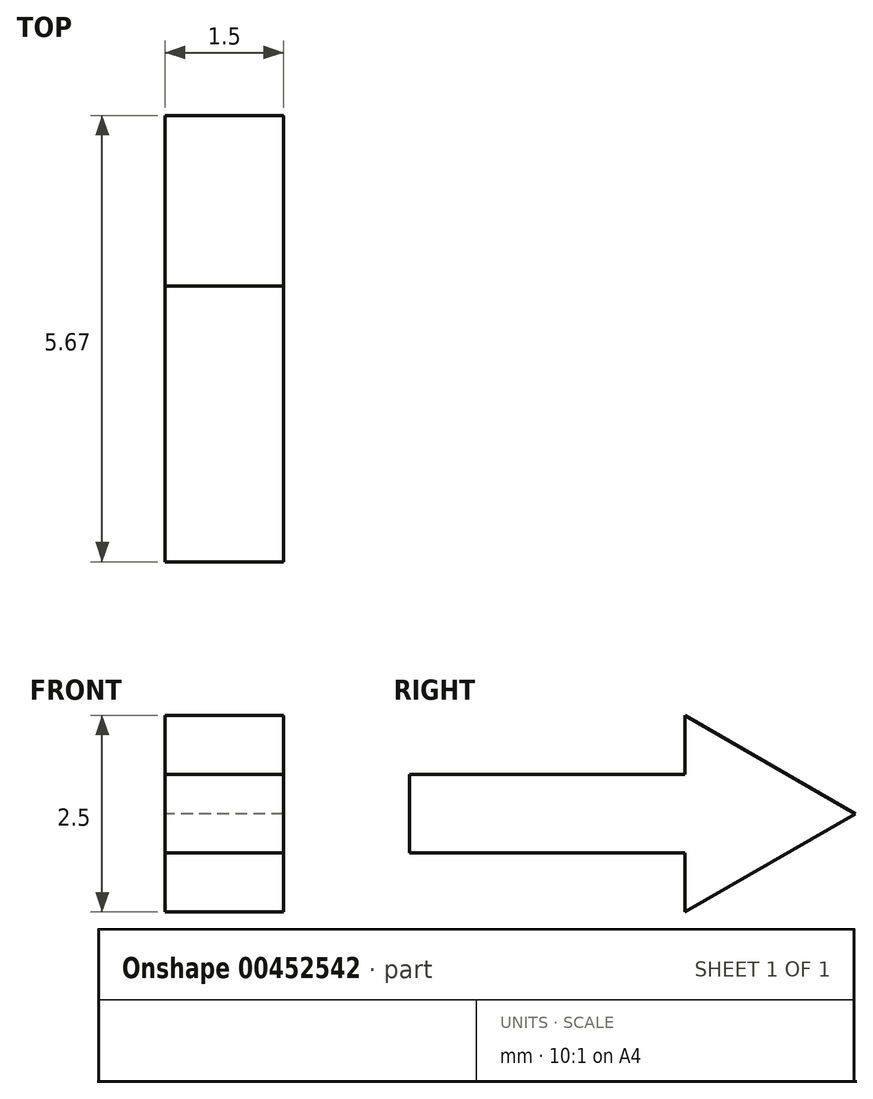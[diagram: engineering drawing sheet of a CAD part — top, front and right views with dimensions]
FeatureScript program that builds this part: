
annotation { "Feature Type Name" : "Feature", "Feature Type Description" : "" }
export const myFeature = defineFeature(function(context is Context, id is Id, definition is map)
    precondition{}
    {
        {
            var Q0;
            Q0=qCreatedBy(makeId("Right.planeOp"),FACE);
            var sketch = newSketch(context, id + "F0", { "sketchPlane" : qUnion([Q0])});
            skLineSegment(sketch, "E0.bottom", {"start": v(-3.5, -0.5) * mm, "end": v(0, -0.5) * mm});
            skLineSegment(sketch, "E0.top", {"start": v(-3.5, 0.5) * mm, "end": v(0, 0.5) * mm});
            skLineSegment(sketch, "E0.left", {"start": v(-3.5, 0.5) * mm, "end": v(-3.5, -0.5) * mm});
            skLineSegment(sketch, "E0.right", {"start": v(0, 0.5) * mm, "end": v(0, -0.5) * mm});
            skLineSegment(sketch, "E1", {"start": v(0, -0.5) * mm, "end": v(0, 1.25) * mm});
            skLineSegment(sketch, "E2", {"start": v(0, 1.25) * mm, "end": v(2.17, 0) * mm});
            skPoint(sketch, "E2.endSnap0", {"position": v(0, 0) * mm});
            skLineSegment(sketch, "E3", {"start": v(2.17, 0) * mm, "end": v(0, -1.25) * mm});
            skLineSegment(sketch, "E4", {"start": v(0, -1.25) * mm, "end": v(0, 0.5) * mm});
            skSolve(sketch);
        }
        {
            var Q0;
            Q0 = qSketchRegion(id + "F0", true);
            extrude(context, id + "F1", {"entities" : qUnion([Q0]), "depth" : 1.5 * mm});
        }
    });
